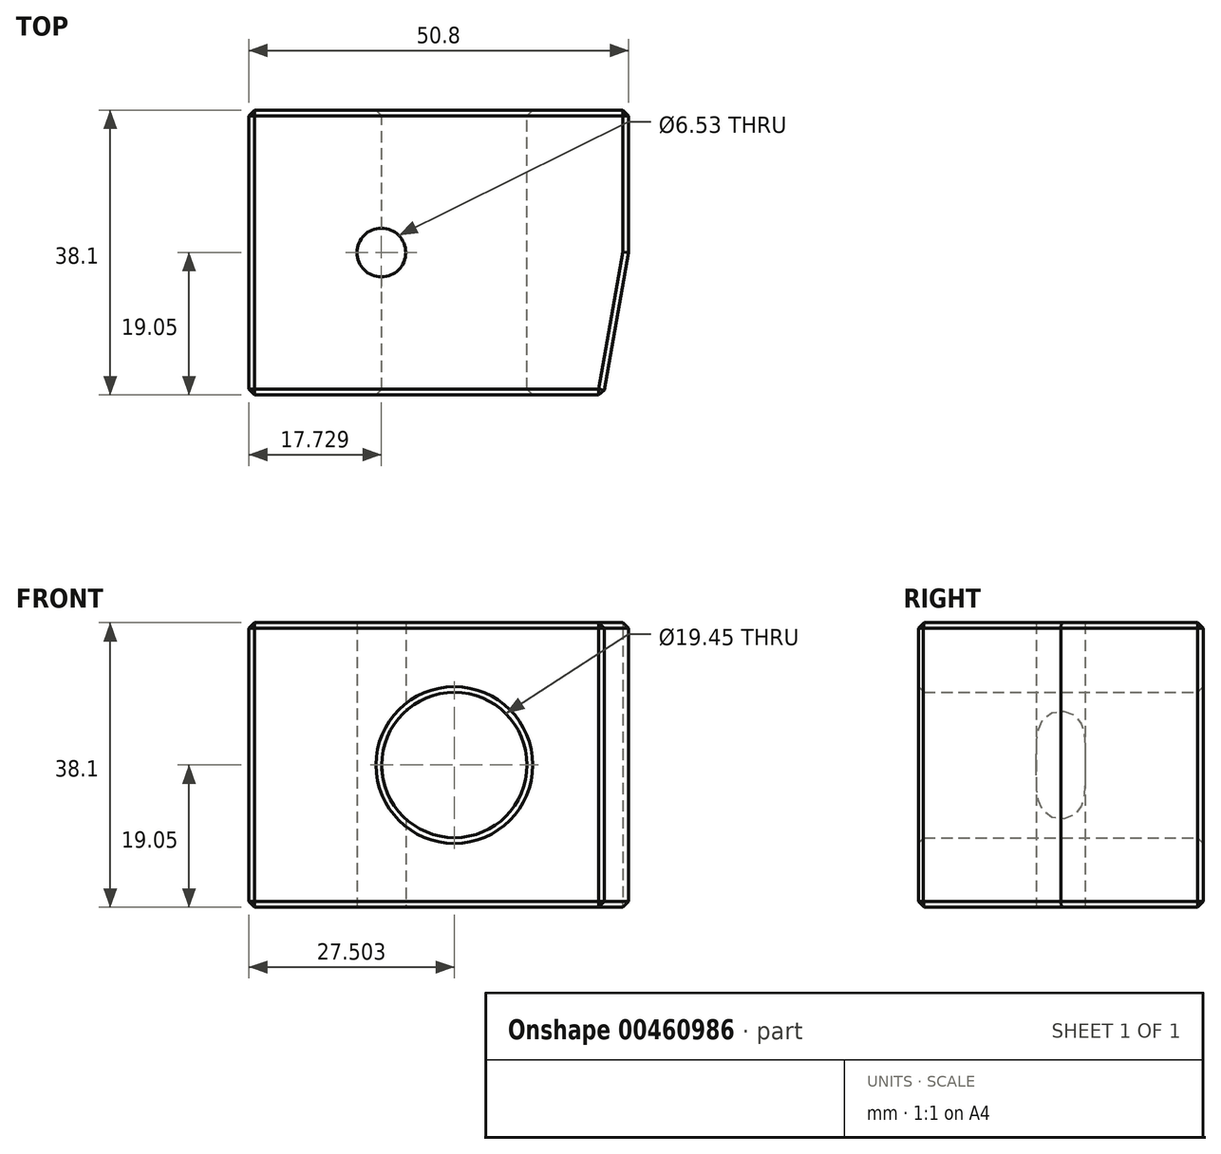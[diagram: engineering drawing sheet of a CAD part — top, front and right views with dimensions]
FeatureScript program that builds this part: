
annotation { "Feature Type Name" : "Feature", "Feature Type Description" : "" }
export const myFeature = defineFeature(function(context is Context, id is Id, definition is map)
    precondition{}
    {
        {
            var Q0;
            Q0=qCreatedBy(makeId("Front.planeOp"),FACE);
            var sketch = newSketch(context, id + "F0", { "sketchPlane" : qUnion([Q0])});
            skLineSegment(sketch, "E0.bottom", {"start": v(25.4, 19.05) * mm, "end": v(-25.4, 19.05) * mm});
            skLineSegment(sketch, "E0.top", {"start": v(25.4, -19.05) * mm, "end": v(-25.4, -19.05) * mm});
            skLineSegment(sketch, "E0.left", {"start": v(25.4, 19.05) * mm, "end": v(25.4, -19.05) * mm});
            skLineSegment(sketch, "E0.right", {"start": v(-25.4, 19.05) * mm, "end": v(-25.4, -19.05) * mm});
            skPoint(sketch, "E0.middle", {"position": v(0, 0) * mm});
            skCircle(sketch, "E1", {"center": v(2.1, 0) * mm, "radius": 9.72 * mm});
            skSolve(sketch);
        }
        {
            var Q0;
            Q0=makeQuery(id+"F0.imprint","IMPRINT",FACE,{"disambiguationData":[TD([[makeQuery(id+"F0.imprint","IMPRINT",EDGE,{"derivedFrom":sQuery(id+"F0.wireOp",EDGE,"E0.bottom")}),1.0]])]});
            extrude(context, id + "F1", {"entities" : qUnion([Q0]), "depth" : 38.1 * mm});
        }
        {
            var Q0;
            Q0=makeQuery(id+"F1.opExtrude","SWEPT_FACE",FACE,{"disambiguationData":[OSD([sQuery(id+"F0.wireOp",EDGE,"E0.top")])]});
            var sketch = newSketch(context, id + "F2", { "sketchPlane" : qUnion([Q0])});
            skPoint(sketch, "E2", {"position": v(-7.67, 19.05) * mm});
            skSolve(sketch);
        }
        {
            var Q0;
            Q0=sQuery(id+"F2.wireOp",VERTEX,"E2");
            var Q1;
            Q1=makeQuery(id+"F1.opExtrude","SWEPT_BODY",BODY,{"disambiguationData":[OSD([sQuery(id+"F0.wireOp",EDGE,"E0.bottom"),sQuery(id+"F0.wireOp",EDGE,"E0.top"),sQuery(id+"F0.wireOp",EDGE,"E0.left"),sQuery(id+"F0.wireOp",EDGE,"E0.right"),sQuery(id+"F0.wireOp",EDGE,"E1")])]});
            hole(context, id + "F3", {"style" : HoleStyle.SIMPLE, "endStyle" : HoleEndStyle.THROUGH, "holeDiameter" : 6.53 * mm, "locations" : qUnion([Q0]), "scope" : qUnion([Q1]), "isTappedThrough" : true});
        }
        {
            var Q0;
            Q0=makeQuery(id+"F1.opExtrude","CAP_EDGE",EDGE,{"disambiguationData":[OSD([sQuery(id+"F0.wireOp",EDGE,"E0.left")])],"isStart":false});
            chamfer(context, id + "F4", {"entities" : qUnion([Q0]), "chamferType" : ChamferType.OFFSET_ANGLE, "width" : 19.05 * mm, "oppositeDirection" : false, "angle" : 10 * degree, "tangentPropagation" : true});
        }
        {
            var Q0;
            Q0=makeQuery(id+"F1.opExtrude","CAP_EDGE",EDGE,{"disambiguationData":[OSD([sQuery(id+"F0.wireOp",EDGE,"E0.top")])],"isStart":false});
            var Q1;
            Q1=makeQuery(id+"F1.opExtrude","CAP_EDGE",EDGE,{"disambiguationData":[OSD([sQuery(id+"F0.wireOp",EDGE,"E0.right")])],"isStart":false});
            var Q2;
            Q2=makeQuery(id+"F1.opExtrude","CAP_EDGE",EDGE,{"disambiguationData":[OSD([sQuery(id+"F0.wireOp",EDGE,"E0.bottom")])],"isStart":false});
            var Q3;
            Q3=makeQuery(id+"F1.opExtrude","SWEPT_EDGE",EDGE,{"disambiguationData":[OSD([sQuery(id+"F0.wireOp",EDGE,"E0.top"),sQuery(id+"F0.wireOp",EDGE,"E0.right")])]});
            var Q4;
            Q4=makeQuery(id+"F1.opExtrude","CAP_EDGE",EDGE,{"disambiguationData":[OSD([sQuery(id+"F0.wireOp",EDGE,"E0.top")])],"isStart":true});
            var Q5;
            Q5=makeQuery(id+"F1.opExtrude","CAP_EDGE",EDGE,{"disambiguationData":[OSD([sQuery(id+"F0.wireOp",EDGE,"E0.left")])],"isStart":true});
            var Q6;
            Q6=makeQuery(id+"F4.opChamfer","BLEND_EDGE",EDGE,{"blendedFrom":[makeQuery(id+"F1.opExtrude","CAP_EDGE",EDGE,{"disambiguationData":[OSD([sQuery(id+"F0.wireOp",EDGE,"E0.left")])],"isStart":false}),makeQuery(id+"F1.opExtrude","SWEPT_FACE",FACE,{"disambiguationData":[OSD([sQuery(id+"F0.wireOp",EDGE,"E0.bottom")])]})],"blendedInto":[makeQuery(id+"F1.opExtrude","SWEPT_FACE",FACE,{"disambiguationData":[OSD([sQuery(id+"F0.wireOp",EDGE,"E0.bottom")])]})]});
            var Q7;
            Q7=makeQuery(id+"F1.opExtrude","SWEPT_EDGE",EDGE,{"disambiguationData":[OSD([sQuery(id+"F0.wireOp",EDGE,"E0.bottom"),sQuery(id+"F0.wireOp",EDGE,"E0.left")])]});
            var Q8;
            Q8=makeQuery(id+"F1.opExtrude","CAP_EDGE",EDGE,{"disambiguationData":[OSD([sQuery(id+"F0.wireOp",EDGE,"E0.bottom")])],"isStart":true});
            var Q9;
            Q9=makeQuery(id+"F1.opExtrude","SWEPT_EDGE",EDGE,{"disambiguationData":[OSD([sQuery(id+"F0.wireOp",EDGE,"E0.bottom"),sQuery(id+"F0.wireOp",EDGE,"E0.right")])]});
            var Q10;
            Q10=makeQuery(id+"F1.opExtrude","CAP_EDGE",EDGE,{"disambiguationData":[OSD([sQuery(id+"F0.wireOp",EDGE,"E0.right")])],"isStart":true});
            var Q11;
            {var subQ0=sQuery(id+"F0.wireOp",EDGE,"E0.left");Q11=makeQuery(id+"F4.opChamfer","BLEND_EDGE",EDGE,{"blendedFrom":[makeQuery(id+"F1.opExtrude","CAP_EDGE",EDGE,{"disambiguationData":[OSD([subQ0])],"isStart":false}),makeQuery(id+"F1.opExtrude","CAP_FACE",FACE,{"disambiguationData":[OSD([sQuery(id+"F0.wireOp",EDGE,"E0.bottom"),sQuery(id+"F0.wireOp",EDGE,"E0.top"),subQ0,sQuery(id+"F0.wireOp",EDGE,"E0.right"),sQuery(id+"F0.wireOp",EDGE,"E1")])],"isStart":false})],"blendedInto":[makeQuery(id+"F1.opExtrude","CAP_FACE",FACE,{"disambiguationData":[OSD([sQuery(id+"F0.wireOp",EDGE,"E0.bottom"),sQuery(id+"F0.wireOp",EDGE,"E0.top"),subQ0,sQuery(id+"F0.wireOp",EDGE,"E0.right"),sQuery(id+"F0.wireOp",EDGE,"E1")])],"isStart":false})]});}
            var Q12;
            Q12=makeQuery(id+"F4.opChamfer","BLEND_EDGE",EDGE,{"blendedFrom":[makeQuery(id+"F1.opExtrude","CAP_EDGE",EDGE,{"disambiguationData":[OSD([sQuery(id+"F0.wireOp",EDGE,"E0.left")])],"isStart":false}),makeQuery(id+"F1.opExtrude","SWEPT_FACE",FACE,{"disambiguationData":[OSD([sQuery(id+"F0.wireOp",EDGE,"E0.top")])]})],"blendedInto":[makeQuery(id+"F1.opExtrude","SWEPT_FACE",FACE,{"disambiguationData":[OSD([sQuery(id+"F0.wireOp",EDGE,"E0.top")])]})]});
            var Q13;
            Q13=makeQuery(id+"F1.opExtrude","SWEPT_EDGE",EDGE,{"disambiguationData":[OSD([sQuery(id+"F0.wireOp",EDGE,"E0.top"),sQuery(id+"F0.wireOp",EDGE,"E0.left")])]});
            var Q14;
            Q14=makeQuery(id+"F1.opExtrude","CAP_EDGE",EDGE,{"disambiguationData":[OSD([sQuery(id+"F0.wireOp",EDGE,"E1")])],"isStart":false});
            var Q15;
            Q15=makeQuery(id+"F3.hole-0.boolean.opBoolean","COPY",EDGE,{"derivedFrom":makeQuery(id+"F3.hole-0.opRevolve","SWEPT_EDGE",EDGE,{"disambiguationData":[OSD([sQuery(id+"F3.hole-0.sketch.wireOp",EDGE,"core_line_2"),sQuery(id+"F3.hole-0.sketch.wireOp",EDGE,"core_line_3")])]})});
            var Q16;
            Q16=makeQuery(id+"F3.hole-0.boolean.opBoolean","INTERSECT",EDGE,{"derivedFrom":[makeQuery(id+"F1.opExtrude","SWEPT_FACE",FACE,{"disambiguationData":[OSD([sQuery(id+"F0.wireOp",EDGE,"E0.bottom")])]}),makeQuery(id+"F3.hole-0.opRevolve","SWEPT_FACE",FACE,{"disambiguationData":[OSD([sQuery(id+"F3.hole-0.sketch.wireOp",EDGE,"core_line_2")])]})]});
            var Q17;
            Q17=makeQuery(id+"F1.opExtrude","CAP_EDGE",EDGE,{"disambiguationData":[OSD([sQuery(id+"F0.wireOp",EDGE,"E1")])],"isStart":true});
            chamfer(context, id + "F5", {"entities" : qUnion([Q0, Q1, Q2, Q3, Q4, Q5, Q6, Q7, Q8, Q9, Q10, Q11, Q12, Q13, Q14, Q15, Q16, Q17]), "width" : 0.76 * mm, "tangentPropagation" : true});
        }
    });
